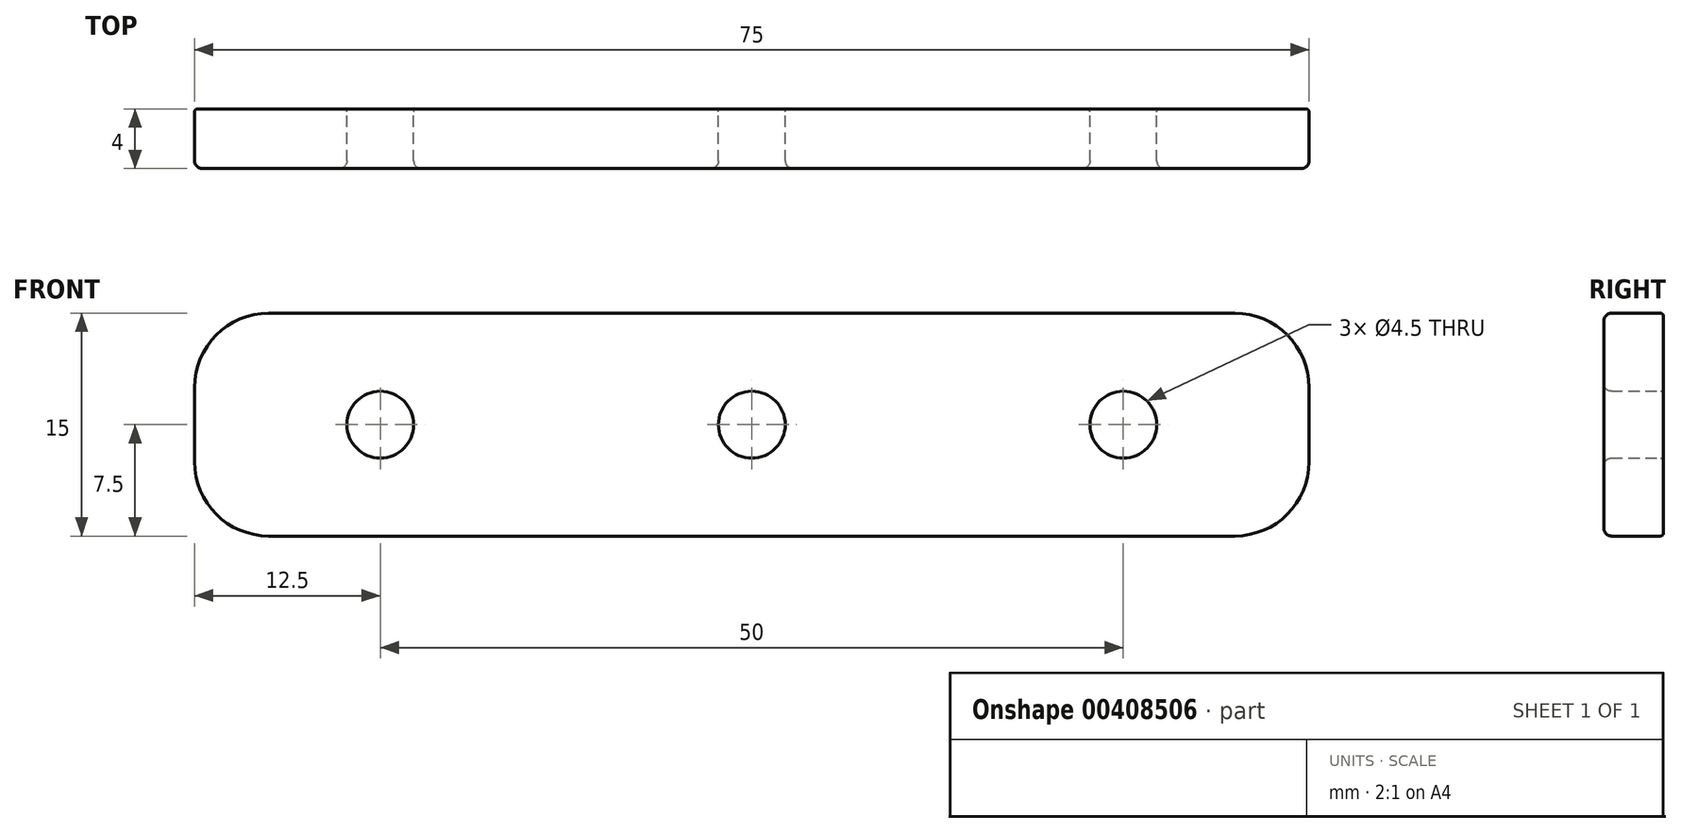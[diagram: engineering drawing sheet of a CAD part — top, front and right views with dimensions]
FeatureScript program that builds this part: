
annotation { "Feature Type Name" : "Feature", "Feature Type Description" : "" }
export const myFeature = defineFeature(function(context is Context, id is Id, definition is map)
    precondition{}
    {
        {
            var Q0;
            Q0=qCreatedBy(makeId("Front.planeOp"),FACE);
            var sketch = newSketch(context, id + "F0", { "sketchPlane" : qUnion([Q0])});
            skLineSegment(sketch, "E0.bottom", {"start": v(32.5, 7.5) * mm, "end": v(-32.5, 7.5) * mm});
            skLineSegment(sketch, "E0.top", {"start": v(32.5, -7.5) * mm, "end": v(-32.5, -7.5) * mm});
            skLineSegment(sketch, "E0.left", {"start": v(37.5, 2.5) * mm, "end": v(37.5, -2.5) * mm});
            skLineSegment(sketch, "E0.right", {"start": v(-37.5, 2.5) * mm, "end": v(-37.5, -2.5) * mm});
            skPoint(sketch, "E0.middle", {"position": v(0, 0) * mm});
            skCircle(sketch, "E1", {"center": v(-25, 0) * mm, "radius": 2.25 * mm});
            skCircle(sketch, "E2.1.0.0", {"center": v(0, 0) * mm, "radius": 2.25 * mm});
            skCircle(sketch, "E2.2.0.0", {"center": v(25, 0) * mm, "radius": 2.25 * mm});
            skLineSegment(sketch, "E2.direction1", {"start": v(-25, 0) * mm, "end": v(0, 0) * mm, "construction": true});
            skPoint(sketch, "E3.visualSharp", {"position": v(-37.5, 7.5) * mm});
            skArc(sketch, "E3.filletArc", {"start": v(-32.5, 7.5) * mm, "mid": v(-36.04, 6.04) * mm, "end": v(-37.5, 2.5) * mm});
            skPoint(sketch, "E4.visualSharp", {"position": v(37.5, 7.5) * mm});
            skArc(sketch, "E4.filletArc", {"start": v(37.5, 2.5) * mm, "mid": v(36.04, 6.04) * mm, "end": v(32.5, 7.5) * mm});
            skPoint(sketch, "E5.visualSharp", {"position": v(37.5, -7.5) * mm});
            skArc(sketch, "E5.filletArc", {"start": v(32.5, -7.5) * mm, "mid": v(36.04, -6.04) * mm, "end": v(37.5, -2.5) * mm});
            skPoint(sketch, "E6.visualSharp", {"position": v(-37.5, -7.5) * mm});
            skArc(sketch, "E6.filletArc", {"start": v(-37.5, -2.5) * mm, "mid": v(-36.04, -6.04) * mm, "end": v(-32.5, -7.5) * mm});
            skSolve(sketch);
        }
        {
            var Q0;
            Q0 = qSketchRegion(id + "F0", true);
            extrude(context, id + "F1", {"entities" : qUnion([Q0]), "depth" : 4 * mm});
        }
        {
            var Q0;
            Q0=makeQuery(id+"F1.opExtrude","CAP_FACE",FACE,{"disambiguationData":[OSD([sQuery(id+"F0.wireOp",EDGE,"E0.bottom"),sQuery(id+"F0.wireOp",EDGE,"E0.top"),sQuery(id+"F0.wireOp",EDGE,"E0.left"),sQuery(id+"F0.wireOp",EDGE,"E0.right"),sQuery(id+"F0.wireOp",EDGE,"E1"),sQuery(id+"F0.wireOp",EDGE,"E2.1.0.0"),sQuery(id+"F0.wireOp",EDGE,"E2.2.0.0"),sQuery(id+"F0.wireOp",EDGE,"E3.filletArc"),sQuery(id+"F0.wireOp",EDGE,"E4.filletArc"),sQuery(id+"F0.wireOp",EDGE,"E5.filletArc"),sQuery(id+"F0.wireOp",EDGE,"E6.filletArc")])],"isStart":false});
            fillet(context, id + "F2", {"entities" : qUnion([Q0]), "radius" : .5 * mm, "tangentPropagation" : true, "allowEdgeOverflow" : false});
        }
        {
            var Q0;
            Q0=makeQuery(id+"F1.opExtrude","CAP_FACE",FACE,{"disambiguationData":[OSD([sQuery(id+"F0.wireOp",EDGE,"E0.bottom"),sQuery(id+"F0.wireOp",EDGE,"E0.top"),sQuery(id+"F0.wireOp",EDGE,"E0.left"),sQuery(id+"F0.wireOp",EDGE,"E0.right"),sQuery(id+"F0.wireOp",EDGE,"E1"),sQuery(id+"F0.wireOp",EDGE,"E2.1.0.0"),sQuery(id+"F0.wireOp",EDGE,"E2.2.0.0"),sQuery(id+"F0.wireOp",EDGE,"E3.filletArc"),sQuery(id+"F0.wireOp",EDGE,"E4.filletArc"),sQuery(id+"F0.wireOp",EDGE,"E5.filletArc"),sQuery(id+"F0.wireOp",EDGE,"E6.filletArc")])],"isStart":true});
            fillet(context, id + "F3", {"entities" : qUnion([Q0]), "radius" : .2 * mm, "tangentPropagation" : true, "allowEdgeOverflow" : false});
        }
    });
